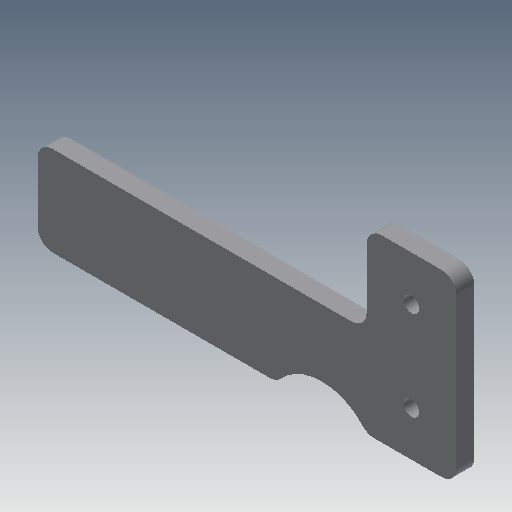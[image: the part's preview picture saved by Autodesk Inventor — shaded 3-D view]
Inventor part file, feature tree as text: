
AUTODESK INVENTOR PART (.ipt)
format: ipt  version: 2017 (Build 210142000, 142)  size: 112,128 bytes
history: native  units: mm
features: extrude x1, sketch x1
ambient origin geometry x8: Origin, YZ Plane, XZ Plane, XY Plane, X Axis, Y Axis, Z Axis, Center Point
bodies: Solid1 (feature_tree)
feature tree (2):
  extrude  "Extrusion1"  Depth=5.0mm
  sketch  "Sketch1"  dims[d5=5.0mm d6=5.0mm d8=5.0mm d9=5.0mm d10=5.0mm d11=5.0mm d12=5.0mm d14=60.0mm d18=5.2mm d19=5.2mm d20=6.0mm d21=0.0mm]
